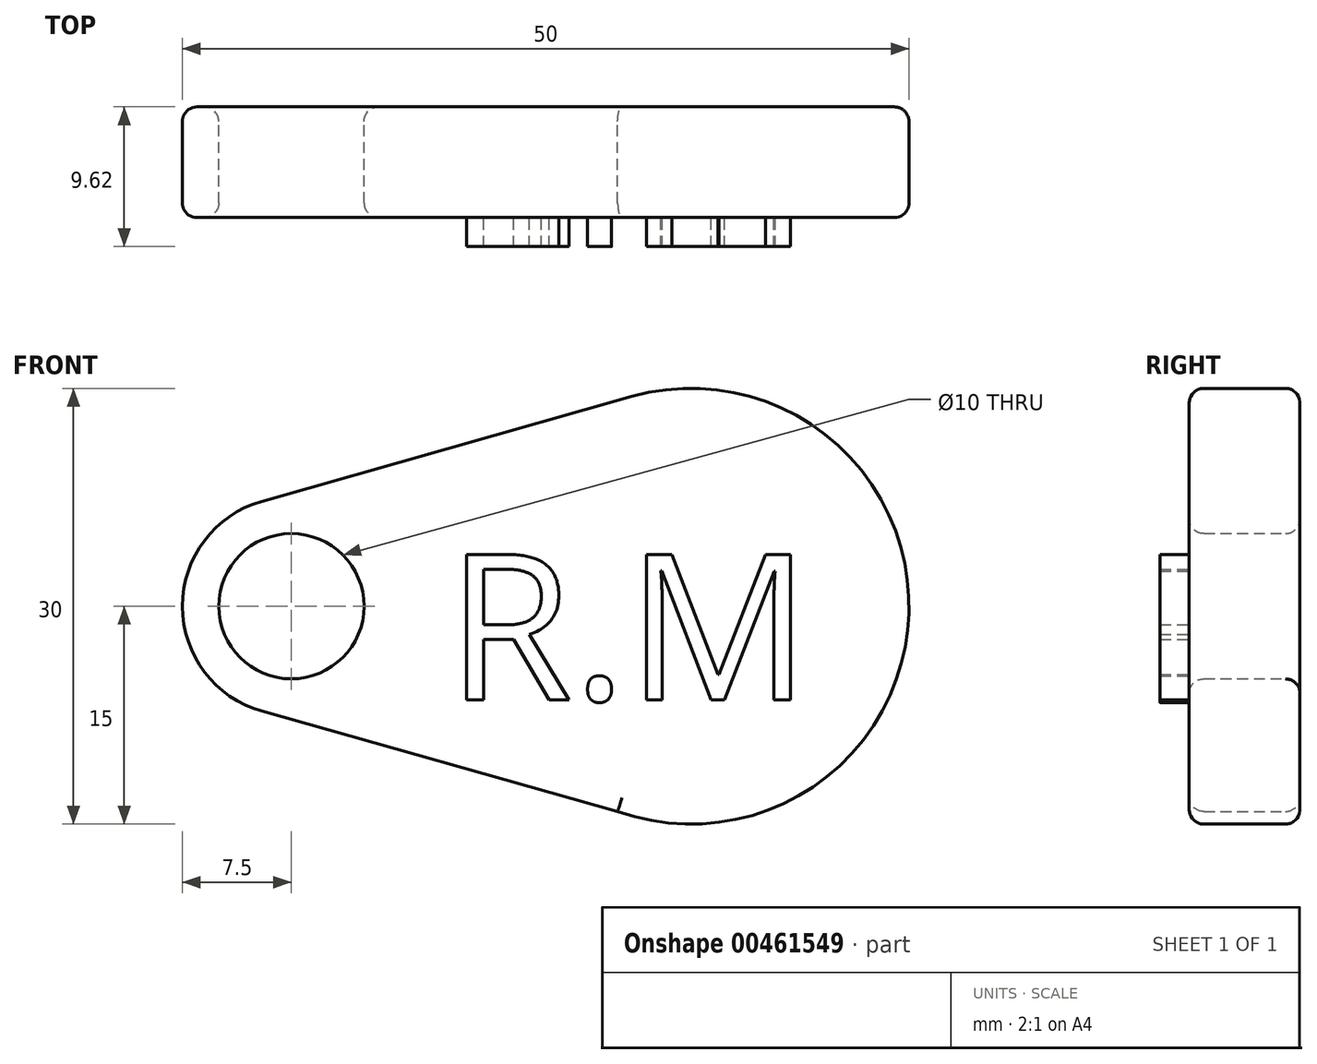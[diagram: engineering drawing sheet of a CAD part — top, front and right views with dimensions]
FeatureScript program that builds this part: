
annotation { "Feature Type Name" : "Feature", "Feature Type Description" : "" }
export const myFeature = defineFeature(function(context is Context, id is Id, definition is map)
    precondition{}
    {
        {
            var Q0;
            Q0=qCreatedBy(makeId("Front.planeOp"),FACE);
            var sketch = newSketch(context, id + "F0", { "sketchPlane" : qUnion([Q0])});
            skCircle(sketch, "E0", {"center": v(0, 0) * mm, "radius": 15 * mm});
            skCircle(sketch, "E1", {"center": v(-27.5, 0) * mm, "radius": 7.5 * mm});
            skLineSegment(sketch, "E2", {"start": v(-29.55, 7.22) * mm, "end": v(-4.09, 14.43) * mm});
            skLineSegment(sketch, "E3", {"start": v(-29.54, -7.22) * mm, "end": v(-3.08, -14.68) * mm});
            skCircle(sketch, "E4", {"center": v(-27.5, 0) * mm, "radius": 5 * mm});
            skSolve(sketch);
        }
        {
            var Q0;
            {var subQ0=sQuery(id+"F0.wireOp",EDGE,"E3");var subQ1=sQuery(id+"F0.wireOp",EDGE,"E0");var subQ2=makeQuery(id+"F0.imprint","INTERSECT",VERTEX,{"disambiguationData":[OD(0.0)],"derivedFrom":[subQ1,subQ0]});Q0=makeQuery(id+"F0.imprint","IMPRINT",FACE,{"disambiguationData":[TD([[makeQuery(id+"F0.imprint","IMPRINT",EDGE,{"disambiguationData":[TD([[subQ2,1.0]])],"derivedFrom":subQ1}),1.0]])]});}
            var Q1;
            {var subQ0=sQuery(id+"F0.wireOp",EDGE,"E2");Q1=makeQuery(id+"F0.imprint","IMPRINT",FACE,{"disambiguationData":[TD([[makeQuery(id+"F0.imprint","IMPRINT",EDGE,{"derivedFrom":subQ0}),-1.0]])]});}
            var Q2;
            Q2=makeQuery(id+"F0.imprint","IMPRINT",FACE,{"disambiguationData":[TD([[makeQuery(id+"F0.imprint","IMPRINT",EDGE,{"derivedFrom":sQuery(id+"F0.wireOp",EDGE,"E4")}),-1.0]])]});
            var Q3;
            {var subQ0=sQuery(id+"F0.wireOp",EDGE,"E0");var subQ1=makeQuery(id+"F0.imprint","INTERSECT",VERTEX,{"derivedFrom":[subQ0,sQuery(id+"F0.wireOp",EDGE,"E2")]});Q3=makeQuery(id+"F0.imprint","IMPRINT",FACE,{"disambiguationData":[TD([[makeQuery(id+"F0.imprint","IMPRINT",EDGE,{"disambiguationData":[TD([[subQ1,-1.0]])],"derivedFrom":subQ0}),1.0]])]});}
            extrude(context, id + "F1", {"entities" : qUnion([Q0, Q1, Q2, Q3]), "depth" : 7.62 * mm});
        }
        {
            var Q0;
            Q0=makeQuery(id+"F1.opExtrude","CAP_FACE",FACE,{"disambiguationData":[OSD([sQuery(id+"F0.wireOp",EDGE,"E0"),sQuery(id+"F0.wireOp",EDGE,"E1"),sQuery(id+"F0.wireOp",EDGE,"E2"),sQuery(id+"F0.wireOp",EDGE,"E3"),sQuery(id+"F0.wireOp",EDGE,"E4")])],"isStart":false});
            var sketch = newSketch(context, id + "F2", { "sketchPlane" : qUnion([Q0])});
            skText(sketch, "E5", { "text": "R.M", "fontName": "OpenSans-Regular.ttf"});
            skPoint(sketch, "E5.firstSnap0", {"position": v(-16.82, 10.82) * mm});
            const initialGuessF2  = {"E5": [-0.01682, -0.00644, 1, 0, 0.01009]};
            skSetInitialGuess(sketch, initialGuessF2);
            skSolve(sketch);
        }
        {
            var Q0;
            Q0 = qSketchRegion(id + "F2", true);
            var Q1;
            Q1 = qSketchRegion(id + "F0", true);
            extrude(context, id + "F3", {"entities" : qUnion([Q0, Q1]), "operationType" : NewBodyOperationType.ADD, "depth" : 2 * mm});
        }
        {
            var Q0;
            Q0=makeQuery(id+"F0.imprint","IMPRINT",FACE,{"disambiguationData":[TD([[makeQuery(id+"F0.imprint","IMPRINT",EDGE,{"derivedFrom":sQuery(id+"F0.wireOp",EDGE,"E4")}),1.0]])]});
            extrude(context, id + "F4", {"entities" : qUnion([Q0]), "operationType" : NewBodyOperationType.REMOVE, "oppositeDirection" : true, "depth" : 10 * mm});
        }
        {
            var Q0;
            Q0=makeQuery(id+"F1.opExtrude","CAP_EDGE",EDGE,{"disambiguationData":[OSD([sQuery(id+"F0.wireOp",EDGE,"E3")])],"isStart":true});
            var Q1;
            Q1=makeQuery(id+"F1.opExtrude","CAP_EDGE",EDGE,{"disambiguationData":[OSD([sQuery(id+"F0.wireOp",EDGE,"E0")])],"isStart":false});
            var Q2;
            Q2=makeQuery(id+"F1.opExtrude","CAP_EDGE",EDGE,{"disambiguationData":[OSD([sQuery(id+"F0.wireOp",EDGE,"E2")])],"isStart":false});
            var Q3;
            Q3=makeQuery(id+"F1.opExtrude","CAP_EDGE",EDGE,{"disambiguationData":[OSD([sQuery(id+"F0.wireOp",EDGE,"E0")])],"isStart":true});
            var Q4;
            Q4=makeQuery(id+"F1.opExtrude","CAP_EDGE",EDGE,{"disambiguationData":[OSD([sQuery(id+"F0.wireOp",EDGE,"E2")])],"isStart":true});
            var Q5;
            Q5=makeQuery(id+"F1.opExtrude","CAP_EDGE",EDGE,{"disambiguationData":[OSD([sQuery(id+"F0.wireOp",EDGE,"E1")])],"isStart":true});
            var Q6;
            Q6=makeQuery(id+"F1.opExtrude","CAP_EDGE",EDGE,{"disambiguationData":[OSD([sQuery(id+"F0.wireOp",EDGE,"E1")])],"isStart":false});
            var Q7;
            Q7=makeQuery(id+"F1.opExtrude","CAP_EDGE",EDGE,{"disambiguationData":[OSD([sQuery(id+"F0.wireOp",EDGE,"E4")])],"isStart":true});
            var Q8;
            Q8=makeQuery(id+"F1.opExtrude","CAP_EDGE",EDGE,{"disambiguationData":[OSD([sQuery(id+"F0.wireOp",EDGE,"E4")])],"isStart":false});
            var Q9;
            Q9=makeQuery(id+"F1.opExtrude","CAP_EDGE",EDGE,{"disambiguationData":[OSD([sQuery(id+"F0.wireOp",EDGE,"E3")])],"isStart":false});
            fillet(context, id + "F5", {"entities" : qUnion([Q0, Q1, Q2, Q3, Q4, Q5, Q6, Q7, Q8, Q9]), "radius" : 1 * mm, "tangentPropagation" : true, "allowEdgeOverflow" : false});
        }
    });
